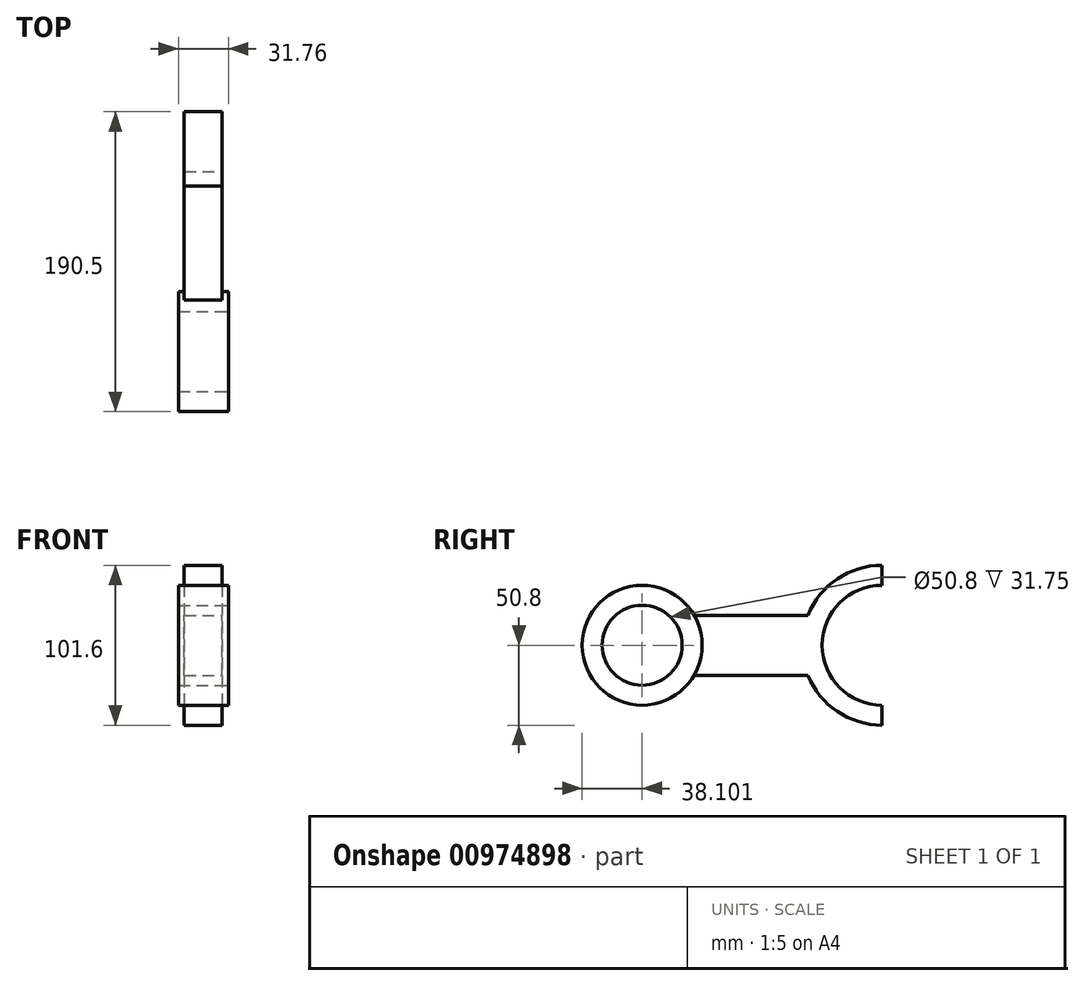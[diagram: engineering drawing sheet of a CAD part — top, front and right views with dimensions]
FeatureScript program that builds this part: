
annotation { "Feature Type Name" : "Feature", "Feature Type Description" : "" }
export const myFeature = defineFeature(function(context is Context, id is Id, definition is map)
    precondition{}
    {
        {
            var Q0;
            Q0=qCreatedBy(makeId("Right.planeOp"),FACE);
            var sketch = newSketch(context, id + "F0", { "sketchPlane" : qUnion([Q0])});
            skLineSegment(sketch, "E0.bottom", {"start": v(63.1, 19.05) * mm, "end": v(-63.1, 19.05) * mm});
            skLineSegment(sketch, "E0.top", {"start": v(63.1, -19.05) * mm, "end": v(-63.1, -19.05) * mm});
            skLineSegment(sketch, "E0.left", {"start": v(63.1, 19.05) * mm, "end": v(63.1, -19.05) * mm, "construction": true});
            skLineSegment(sketch, "E0.right", {"start": v(-63.1, 19.05) * mm, "end": v(-63.1, -19.05) * mm, "construction": true});
            skPoint(sketch, "E0.middle", {"position": v(0, 0) * mm});
            skLineSegment(sketch, "E1", {"start": v(-79.9, 0) * mm, "end": v(72.5, 0) * mm, "construction": true});
            skCircle(sketch, "E2", {"center": v(-79.9, 0) * mm, "radius": 25.4 * mm});
            skCircle(sketch, "E3.0", {"center": v(-79.9, 0) * mm, "radius": 38.1 * mm});
            skArc(sketch, "E4", {"start": v(72.5, 38.1) * mm, "mid": v(34.4, 0) * mm, "end": v(72.5, -38.1) * mm});
            skArc(sketch, "E5.0", {"start": v(72.5, 50.8) * mm, "mid": v(21.7, 0) * mm, "end": v(72.5, -50.8) * mm});
            skLineSegment(sketch, "E6", {"start": v(72.5, 0) * mm, "end": v(72.5, 70.83) * mm, "construction": true});
            skLineSegment(sketch, "E7", {"start": v(72.5, 0) * mm, "end": v(72.5, -59.54) * mm, "construction": true});
            skLineSegment(sketch, "E8", {"start": v(72.5, 50.8) * mm, "end": v(72.5, 38.1) * mm});
            skLineSegment(sketch, "E9", {"start": v(72.5, -38.1) * mm, "end": v(72.5, -50.8) * mm});
            skSolve(sketch);
        }
        {
            var Q0;
            Q0 = qSketchRegion(id + "F0", true);
            extrude(context, id + "F1", {"entities" : qUnion([Q0]), "endBound" : BoundingType.SYMMETRIC, "oppositeDirection" : true, "depth" : 24.13 * mm, "offsetDistance" : 25 * mm});
        }
        {
            var Q0;
            Q0=qCreatedBy(makeId("Right.planeOp"),FACE);
            var sketch = newSketch(context, id + "F2", { "sketchPlane" : qUnion([Q0])});
            skCircle(sketch, "E10", {"center": v(-79.9, 0) * mm, "radius": 25.4 * mm});
            skCircle(sketch, "E11", {"center": v(-79.9, 0) * mm, "radius": 38.1 * mm});
            skSolve(sketch);
        }
        {
            var Q0;
            Q0 = qSketchRegion(id + "F2", true);
            extrude(context, id + "F3", {"entities" : qUnion([Q0]), "operationType" : NewBodyOperationType.ADD, "endBound" : BoundingType.SYMMETRIC, "depth" : 31.75 * mm, "offsetDistance" : 25 * mm});
        }
    });
